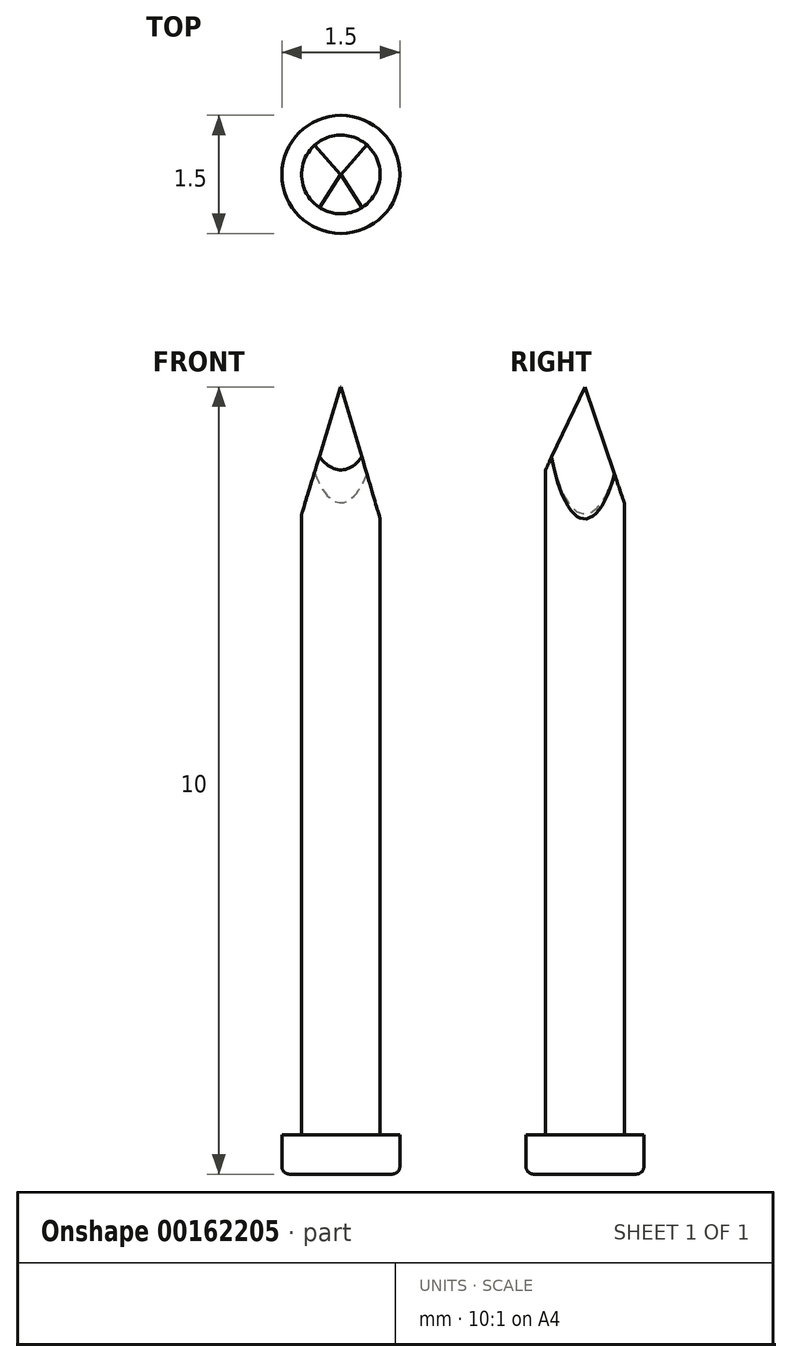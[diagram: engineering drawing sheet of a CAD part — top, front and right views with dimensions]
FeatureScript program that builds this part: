
annotation { "Feature Type Name" : "Feature", "Feature Type Description" : "" }
export const myFeature = defineFeature(function(context is Context, id is Id, definition is map)
    precondition{}
    {
        {
            var Q0;
            Q0=qCreatedBy(makeId("Top.planeOp"),FACE);
            var sketch = newSketch(context, id + "F0", { "sketchPlane" : qUnion([Q0])});
            skCircle(sketch, "E0", {"center": v(0, 0) * mm, "radius": 0.75 * mm});
            skCircle(sketch, "E1", {"center": v(0, 0) * mm, "radius": 0.5 * mm});
            skSolve(sketch);
        }
        {
            var Q0;
            Q0=makeQuery(id+"F0.imprint","IMPRINT",FACE,{"disambiguationData":[TD([[makeQuery(id+"F0.imprint","IMPRINT",EDGE,{"derivedFrom":sQuery(id+"F0.wireOp",EDGE,"E1")}),1.0]])]});
            extrude(context, id + "F1", {"entities" : qUnion([Q0]), "depth" : 10 * mm});
        }
        {
            var Q0;
            Q0=makeQuery(id+"F0.imprint","IMPRINT",FACE,{"disambiguationData":[TD([[makeQuery(id+"F0.imprint","IMPRINT",EDGE,{"derivedFrom":sQuery(id+"F0.wireOp",EDGE,"E0")}),1.0]])]});
            extrude(context, id + "F2", {"entities" : qUnion([Q0]), "operationType" : NewBodyOperationType.ADD, "depth" : 0.5 * mm});
        }
        {
            var Q0;
            Q0=makeQuery(id+"F2.opExtrude","CAP_EDGE",EDGE,{"disambiguationData":[OSD([sQuery(id+"F0.wireOp",EDGE,"E0")])],"isStart":true});
            fillet(context, id + "F3", {"entities" : qUnion([Q0]), "radius" : 0.1 * mm, "tangentPropagation" : true, "allowEdgeOverflow" : false});
        }
        {
            var Q0;
            Q0=qCreatedBy(makeId("Right.planeOp"),FACE);
            var sketch = newSketch(context, id + "F4", { "sketchPlane" : qUnion([Q0])});
            skLineSegment(sketch, "E2", {"start": v(0, 10) * mm, "end": v(0.87, 7.45) * mm});
            skLineSegment(sketch, "E3", {"start": v(0.87, 7.45) * mm, "end": v(0.87, 10.82) * mm});
            skLineSegment(sketch, "E4", {"start": v(0.88, 10.82) * mm, "end": v(-1.21, 10.82) * mm});
            skLineSegment(sketch, "E5", {"start": v(-1.21, 10.82) * mm, "end": v(-1.21, 7.5) * mm});
            skLineSegment(sketch, "E6", {"start": v(0, 10) * mm, "end": v(-1.21, 7.45) * mm});
            skLineSegment(sketch, "E7", {"start": v(-1.21, 7.5) * mm, "end": v(-1.21, 7.45) * mm});
            skSolve(sketch);
        }
        {
            var Q0;
            Q0=makeQuery(id+"F4.imprint","IMPRINT",FACE,{"disambiguationData":[TD([[makeQuery(id+"F4.imprint","IMPRINT",EDGE,{"derivedFrom":sQuery(id+"F4.wireOp",EDGE,"E2")}),1.0]])]});
            extrude(context, id + "F5", {"entities" : qUnion([Q0]), "operationType" : NewBodyOperationType.REMOVE, "oppositeDirection" : true, "depth" : 25 * mm, "hasSecondDirection" : true, "secondDirectionOppositeDirection" : false, "secondDirectionDepth" : 25 * mm});
        }
        {
            var Q0;
            Q0=qCreatedBy(makeId("Front.planeOp"),FACE);
            var sketch = newSketch(context, id + "F6", { "sketchPlane" : qUnion([Q0])});
            skLineSegment(sketch, "E8", {"start": v(0, 10) * mm, "end": v(0.86, 7.12) * mm});
            skLineSegment(sketch, "E9", {"start": v(-0.89, 7.12) * mm, "end": v(0, 10) * mm});
            skLineSegment(sketch, "E10", {"start": v(-0.89, 7.12) * mm, "end": v(-0.89, 10.5) * mm});
            skLineSegment(sketch, "E11", {"start": v(-0.89, 10.5) * mm, "end": v(1.1, 10.5) * mm});
            skLineSegment(sketch, "E12", {"start": v(1.1, 10.5) * mm, "end": v(0.86, 7.12) * mm});
            skSolve(sketch);
        }
        {
            var Q0;
            Q0=makeQuery(id+"F6.imprint","IMPRINT",FACE,{"disambiguationData":[TD([[makeQuery(id+"F6.imprint","IMPRINT",EDGE,{"derivedFrom":sQuery(id+"F6.wireOp",EDGE,"E8")}),1.0]])]});
            extrude(context, id + "F7", {"entities" : qUnion([Q0]), "operationType" : NewBodyOperationType.REMOVE, "depth" : 25 * mm, "hasSecondDirection" : true, "secondDirectionOppositeDirection" : true, "secondDirectionDepth" : 25 * mm});
        }
    });
